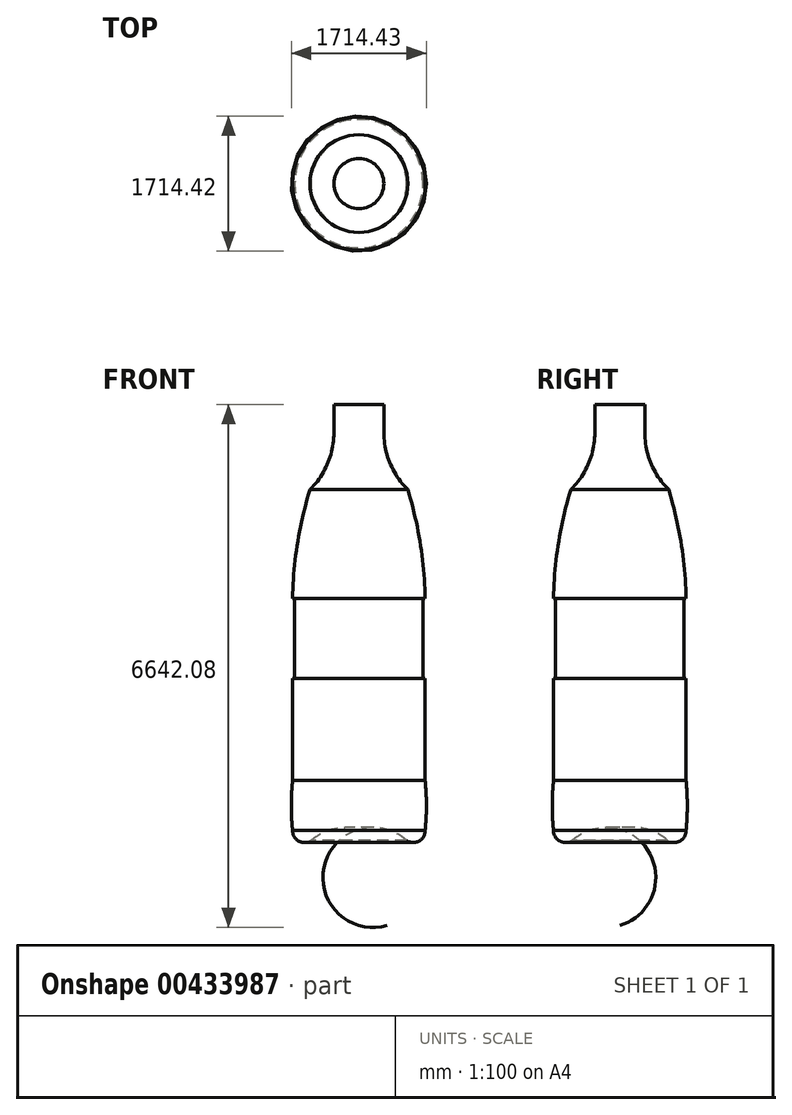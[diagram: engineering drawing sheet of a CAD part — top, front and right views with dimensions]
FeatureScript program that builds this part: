
annotation { "Feature Type Name" : "Feature", "Feature Type Description" : "" }
export const myFeature = defineFeature(function(context is Context, id is Id, definition is map)
    precondition{}
    {
        {
            var Q0;
            Q0=qCreatedBy(makeId("Front.planeOp"),FACE);
            var sketch = newSketch(context, id + "F0", { "sketchPlane" : qUnion([Q0])});
            skLineSegment(sketch, "E0", {"start": v(91.07, 1657.2) * mm, "end": v(91.07, -3740.3) * mm});
            skLineSegment(sketch, "E1", {"start": v(91.07, 1657.2) * mm, "end": v(-226.43, 1657.2) * mm});
            skLineSegment(sketch, "E2", {"start": v(-226.43, 1657.2) * mm, "end": v(-226.43, 1301.6) * mm});
            skPoint(sketch, "E3.endSnap0", {"position": v(-226.43, 1479.4) * mm});
            skArc(sketch, "E4", {"start": v(-530.19, 577.06) * mm, "mid": v(-305.44, 908.79) * mm, "end": v(-226.43, 1301.6) * mm});
            skArc(sketch, "E5", {"start": v(-530.19, 577.06) * mm, "mid": v(-688.76, -106.79) * mm, "end": v(-751.56, -805.97) * mm});
            skArc(sketch, "E6", {"start": v(-751.56, -3754.4) * mm, "mid": v(-672.2, -3888.15) * mm, "end": v(-516.78, -3882.62) * mm});
            skPoint(sketch, "E7.endSnap0", {"position": v(-672.2, -3888.15) * mm});
            skArc(sketch, "E8", {"start": v(91.07, -3740.3) * mm, "mid": v(-231.56, -3731.6) * mm, "end": v(-516.78, -3882.62) * mm});
            skLineSegment(sketch, "E9", {"start": v(-751.56, -1821.97) * mm, "end": v(-751.56, -3119.4) * mm});
            skArc(sketch, "E10", {"start": v(-751.56, -3119.4) * mm, "mid": v(-766.15, -3436.9) * mm, "end": v(-751.56, -3754.4) * mm});
            skLineSegment(sketch, "E11", {"start": v(-723.62, -805.97) * mm, "end": v(-723.62, -1821.97) * mm});
            skLineSegment(sketch, "E12", {"start": v(-723.62, -1821.97) * mm, "end": v(-751.56, -1821.97) * mm});
            skLineSegment(sketch, "E13", {"start": v(-723.62, -805.97) * mm, "end": v(-751.56, -805.97) * mm});
            skSolve(sketch);
        }
        {
            var Q0;
            Q0=makeQuery(id+"F0.imprint","IMPRINT",FACE,{"disambiguationData":[TD([[makeQuery(id+"F0.imprint","IMPRINT",EDGE,{"derivedFrom":sQuery(id+"F0.wireOp",EDGE,"E0")}),-1.0]])]});
            var Q1;
            Q1=sQuery(id+"F0.wireOp",EDGE,"E0");
            revolve(context, id + "F1", {"entities" : qUnion([Q0]), "axis" : qUnion([Q1]), "revolveType" : RevolveType.FULL});
        }
    });
